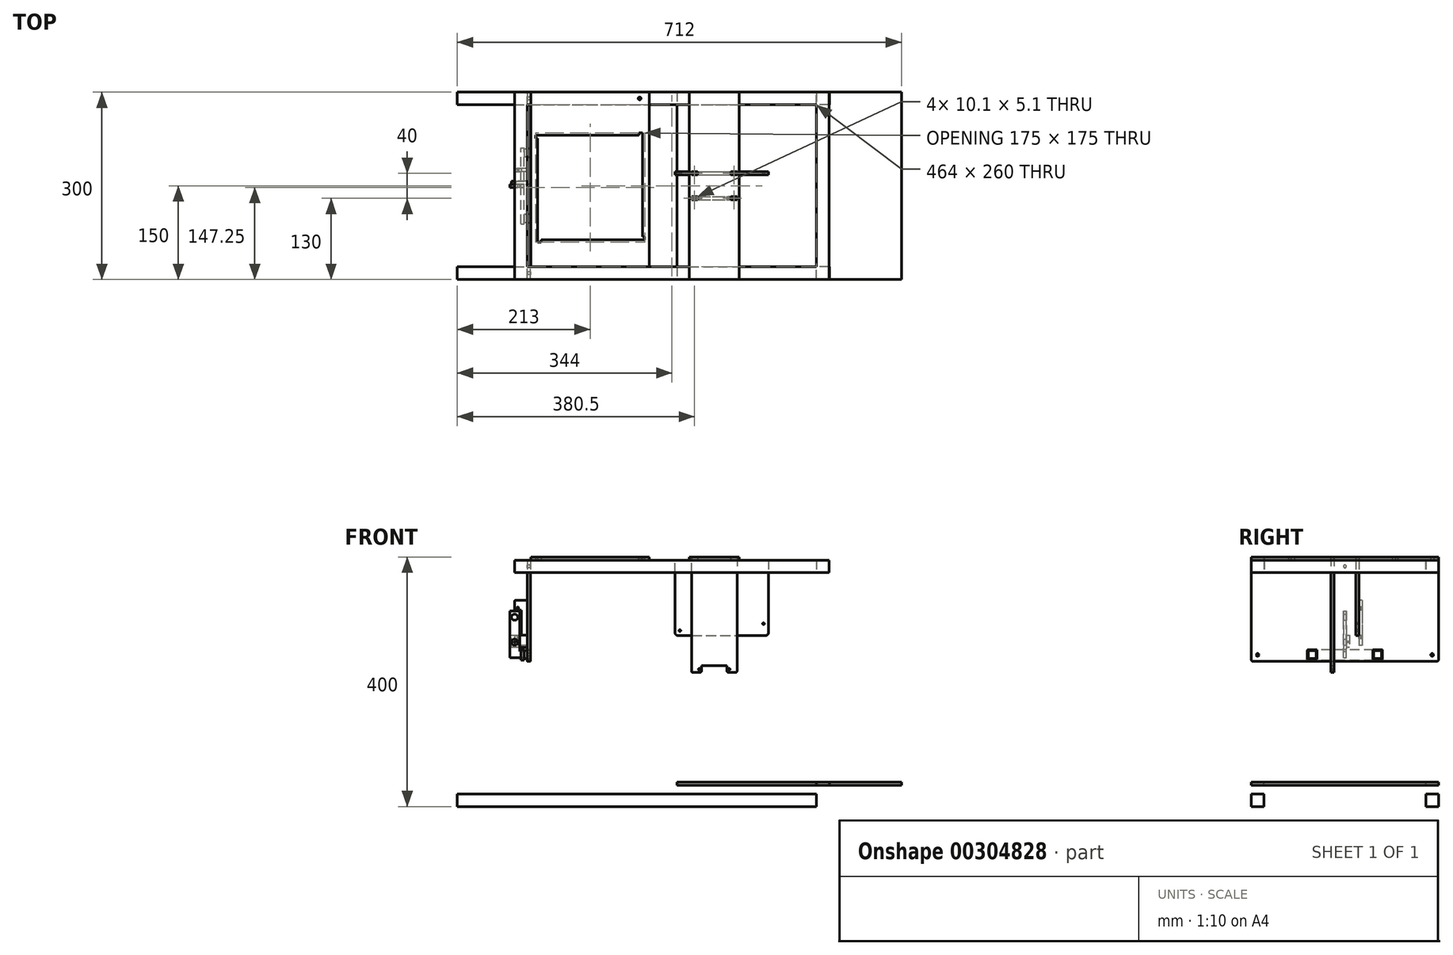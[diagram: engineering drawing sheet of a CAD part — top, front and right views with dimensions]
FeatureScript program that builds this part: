
annotation { "Feature Type Name" : "Feature", "Feature Type Description" : "" }
export const myFeature = defineFeature(function(context is Context, id is Id, definition is map)
    precondition{}
    {
        {
            var Q0;
            Q0=qCreatedBy(makeId("Front.planeOp"),FACE);
            var sketch = newSketch(context, id + "F0", { "sketchPlane" : qUnion([Q0])});
            skLineSegment(sketch, "E0", {"start": v(-53, 64) * mm, "end": v(-53, 180) * mm});
            skCircle(sketch, "E1", {"center": v(-45, 67) * mm, "radius": 1.4 * mm});
            skCircle(sketch, "E2", {"center": v(89, 78) * mm, "radius": 1.4 * mm});
            skLineSegment(sketch, "E3", {"start": v(97, 180) * mm, "end": v(97, 64) * mm});
            skLineSegment(sketch, "E4", {"start": v(-48, 59) * mm, "end": v(92, 59) * mm});
            skArc(sketch, "E5.filletArc", {"start": v(-53, 64) * mm, "mid": v(-51.54, 60.46) * mm, "end": v(-48, 59) * mm});
            skArc(sketch, "E6.filletArc", {"start": v(92, 59) * mm, "mid": v(95.54, 60.46) * mm, "end": v(97, 64) * mm});
            skPoint(sketch, "E7", {"position": v(0, 0) * mm});
            skLineSegment(sketch, "E8", {"start": v(-26.5, 180) * mm, "end": v(-26.5, 185) * mm});
            skLineSegment(sketch, "E9", {"start": v(-26.5, 185) * mm, "end": v(-16.5, 185) * mm});
            skLineSegment(sketch, "E10", {"start": v(-16.5, 185) * mm, "end": v(-16.5, 180) * mm});
            skLineSegment(sketch, "E11", {"start": v(-16.5, 180) * mm, "end": v(36.5, 180) * mm});
            skLineSegment(sketch, "E12", {"start": v(36.5, 180) * mm, "end": v(36.5, 185) * mm});
            skLineSegment(sketch, "E13", {"start": v(36.5, 185) * mm, "end": v(46.5, 185) * mm});
            skLineSegment(sketch, "E14", {"start": v(46.5, 185) * mm, "end": v(46.5, 180) * mm});
            skLineSegment(sketch, "E15", {"start": v(97, 180) * mm, "end": v(46.5, 180) * mm});
            skLineSegment(sketch, "E16", {"start": v(-26.5, 180) * mm, "end": v(-53, 180) * mm});
            skSolve(sketch);
        }
        {
            var Q0;
            Q0=qCreatedBy(makeId("Front.planeOp"),FACE);
            cPlane(context, id + "F1", {"entities" : qUnion([Q0]), "cplaneType" : CPlaneType.OFFSET, "offset" : (17 + 18) * mm, "width" : 150 * mm, "height" : 150 * mm});
        }
        {
            var Q0;
            Q0=qCreatedBy(id+"F1.planeOp",FACE);
            var sketch = newSketch(context, id + "F2", { "sketchPlane" : qUnion([Q0])});
            skCircle(sketch, "E17", {"center": v(-14, 5) * mm, "radius": 1.4 * mm});
            skCircle(sketch, "E18", {"center": v(34, 5) * mm, "radius": 1.4 * mm});
            skLineSegment(sketch, "E19", {"start": v(-24.5, 0) * mm, "end": v(-12.5, 0) * mm});
            skLineSegment(sketch, "E20.trimOffspring", {"start": v(32.5, 0) * mm, "end": v(44.5, 0) * mm});
            skLineSegment(sketch, "E21.top", {"start": v(-10.5, 11) * mm, "end": v(30.5, 11) * mm});
            skLineSegment(sketch, "E21.left", {"start": v(-10.5, 2) * mm, "end": v(-10.5, 11) * mm});
            skLineSegment(sketch, "E21.right", {"start": v(30.5, 2) * mm, "end": v(30.5, 11) * mm});
            skPoint(sketch, "E21.middle", {"position": v(10, 5.5) * mm});
            skLineSegment(sketch, "E22", {"start": v(-26.5, 2) * mm, "end": v(-26.5, 180) * mm});
            skLineSegment(sketch, "E23", {"start": v(46.5, 100) * mm, "end": v(46.5, 2) * mm});
            skPoint(sketch, "E24.visualSharp", {"position": v(-26.5, 0) * mm});
            skArc(sketch, "E24.filletArc", {"start": v(-26.5, 2) * mm, "mid": v(-25.91, 0.59) * mm, "end": v(-24.5, 0) * mm});
            skPoint(sketch, "E25.visualSharp", {"position": v(-10.5, 0) * mm});
            skArc(sketch, "E25.filletArc", {"start": v(-12.5, 0) * mm, "mid": v(-11.09, 0.59) * mm, "end": v(-10.5, 2) * mm});
            skPoint(sketch, "E26.visualSharp", {"position": v(30.5, 0) * mm});
            skArc(sketch, "E26.filletArc", {"start": v(30.5, 2) * mm, "mid": v(31.09, 0.59) * mm, "end": v(32.5, 0) * mm});
            skPoint(sketch, "E27.visualSharp", {"position": v(46.5, 0) * mm});
            skArc(sketch, "E27.filletArc", {"start": v(44.5, 0) * mm, "mid": v(45.91, 0.59) * mm, "end": v(46.5, 2) * mm});
            skLineSegment(sketch, "E28", {"start": v(-26.5, 180) * mm, "end": v(-26.5, 185) * mm});
            skLineSegment(sketch, "E29", {"start": v(-26.5, 185) * mm, "end": v(-16.5, 185) * mm});
            skLineSegment(sketch, "E30", {"start": v(-16.5, 185) * mm, "end": v(-16.5, 180) * mm});
            skLineSegment(sketch, "E31", {"start": v(-16.5, 180) * mm, "end": v(36.5, 180) * mm});
            skLineSegment(sketch, "E32", {"start": v(36.5, 180) * mm, "end": v(36.5, 185) * mm});
            skLineSegment(sketch, "E33", {"start": v(36.5, 185) * mm, "end": v(46.5, 185) * mm});
            skLineSegment(sketch, "E34", {"start": v(46.5, 185) * mm, "end": v(46.5, 100) * mm});
            skLineSegment(sketch, "E35.bottom", {"start": v(-26.5, 200) * mm, "end": v(46.5, 200) * mm});
            skLineSegment(sketch, "E35.top", {"start": v(-26.5, 500) * mm, "end": v(46.5, 500) * mm});
            skLineSegment(sketch, "E35.left", {"start": v(-26.5, 200) * mm, "end": v(-26.5, 327.4) * mm});
            skLineSegment(sketch, "E35.right", {"start": v(46.5, 200) * mm, "end": v(46.5, 327.4) * mm});
            skPoint(sketch, "E36", {"position": v(-26.5, 350) * mm});
            skPoint(sketch, "E37", {"position": v(46.5, 350) * mm});
            skLineSegment(sketch, "E38.bottom", {"start": v(-26.5, 372.6) * mm, "end": v(-16.4, 372.6) * mm});
            skLineSegment(sketch, "E38.top", {"start": v(-26.5, 367.5) * mm, "end": v(-16.4, 367.5) * mm});
            skLineSegment(sketch, "E38.right", {"start": v(-16.4, 372.6) * mm, "end": v(-16.4, 367.5) * mm});
            skLineSegment(sketch, "E39.bottom", {"start": v(46.5, 367.5) * mm, "end": v(36.4, 367.5) * mm});
            skLineSegment(sketch, "E39.top", {"start": v(46.5, 372.6) * mm, "end": v(36.4, 372.6) * mm});
            skLineSegment(sketch, "E39.right", {"start": v(36.4, 367.5) * mm, "end": v(36.4, 372.6) * mm});
            skLineSegment(sketch, "E40.bottom", {"start": v(46.5, 332.5) * mm, "end": v(36.4, 332.5) * mm});
            skLineSegment(sketch, "E40.top", {"start": v(46.5, 327.4) * mm, "end": v(36.4, 327.4) * mm});
            skLineSegment(sketch, "E40.right", {"start": v(36.4, 332.5) * mm, "end": v(36.4, 327.4) * mm});
            skLineSegment(sketch, "E41.bottom", {"start": v(-26.5, 332.5) * mm, "end": v(-16.4, 332.5) * mm});
            skLineSegment(sketch, "E41.top", {"start": v(-26.5, 327.4) * mm, "end": v(-16.4, 327.4) * mm});
            skLineSegment(sketch, "E41.right", {"start": v(-16.4, 332.5) * mm, "end": v(-16.4, 327.4) * mm});
            skLineSegment(sketch, "E42.trimOffspring", {"start": v(-26.5, 372.6) * mm, "end": v(-26.5, 500) * mm});
            skLineSegment(sketch, "E43.trimOffspring", {"start": v(-26.5, 332.5) * mm, "end": v(-26.5, 367.5) * mm});
            skLineSegment(sketch, "E44.trimOffspring", {"start": v(46.5, 372.6) * mm, "end": v(46.5, 500) * mm});
            skLineSegment(sketch, "E45.trimOffspring", {"start": v(46.5, 332.5) * mm, "end": v(46.5, 367.5) * mm});
            skPoint(sketch, "E46", {"position": v(0, 0) * mm});
            skSolve(sketch);
        }
        {
            var Q0;
            Q0=makeQuery(id+"F2.imprint","IMPRINT",FACE,{"disambiguationData":[TD([[makeQuery(id+"F2.imprint","IMPRINT",EDGE,{"derivedFrom":sQuery(id+"F2.wireOp",EDGE,"E17")}),-1.0]])]});
            extrude(context, id + "F3", {"entities" : qUnion([Q0]), "depth" : 5 * mm});
        }
        {
            var Q0;
            Q0=makeQuery(id+"F0.imprint","IMPRINT",FACE,{"disambiguationData":[TD([[makeQuery(id+"F0.imprint","IMPRINT",EDGE,{"derivedFrom":sQuery(id+"F0.wireOp",EDGE,"E0")}),-1.0]])]});
            extrude(context, id + "F4", {"entities" : qUnion([Q0]), "oppositeDirection" : true, "depth" : 5 * mm});
        }
        {
            var Q0;
            Q0=qCreatedBy(id+"F1.planeOp",FACE);
            var sketch = newSketch(context, id + "F5", { "sketchPlane" : qUnion([Q0])});
            skPoint(sketch, "E47", {"position": v(-12.33, -156.3) * mm});
            skPoint(sketch, "E48", {"position": v(-265.6, 28.34) * mm});
            skPoint(sketch, "E49", {"position": v(185.46, 123.56) * mm});
            skLineSegment(sketch, "E50.bottom", {"start": v(-17.83, -156.3) * mm, "end": v(3.17, -156.3) * mm});
            skLineSegment(sketch, "E50.top", {"start": v(-17.83, -151.3) * mm, "end": v(3.17, -151.3) * mm});
            skLineSegment(sketch, "E50.left", {"start": v(-17.83, -156.3) * mm, "end": v(-17.83, -151.3) * mm});
            skLineSegment(sketch, "E50.right", {"start": v(3.17, -156.3) * mm, "end": v(3.17, -151.3) * mm});
            skCircle(sketch, "E51", {"center": v(185.46, 123.56) * mm, "radius": 6 * mm});
            skPoint(sketch, "E52", {"position": v(132.1, 171.6) * mm});
            skCircle(sketch, "E53", {"center": v(132.1, 171.6) * mm, "radius": 6 * mm});
            skSolve(sketch);
        }
        {
            var Q0;
            Q0=qCreatedBy(makeId("Top.planeOp"),FACE);
            cPlane(context, id + "F6", {"entities" : qUnion([Q0]), "cplaneType" : CPlaneType.OFFSET, "offset" : 176 * mm, "oppositeDirection" : true, "width" : 150 * mm, "height" : 150 * mm});
        }
        {
            var Q0;
            Q0=qCreatedBy(id+"F6.planeOp",FACE);
            var sketch = newSketch(context, id + "F7", { "sketchPlane" : qUnion([Q0])});
            skPoint(sketch, "E54", {"position": v(310, -10) * mm});
            skLineSegment(sketch, "E55.top", {"start": v(173.5, 132.5) * mm, "end": v(-50, 132.5) * mm});
            skLineSegment(sketch, "E56.top", {"start": v(173.5, -167.5) * mm, "end": v(-50, -167.5) * mm});
            skLineSegment(sketch, "E57", {"start": v(-50, 132.5) * mm, "end": v(-50, -167.5) * mm});
            skLineSegment(sketch, "E58", {"start": v(310, 132.5) * mm, "end": v(310, -167.5) * mm});
            skPoint(sketch, "E59", {"position": v(310, -17.5) * mm});
            skLineSegment(sketch, "E60.top", {"start": v(194.5, 112.5) * mm, "end": v(173.5, 112.5) * mm});
            skLineSegment(sketch, "E60.right", {"start": v(173.5, 132.5) * mm, "end": v(173.5, 112.5) * mm});
            skPoint(sketch, "E60.left.start.orphan", {"position": v(310, 132.5) * mm});
            skLineSegment(sketch, "E61.top", {"start": v(194.5, -147.5) * mm, "end": v(173.5, -147.5) * mm});
            skLineSegment(sketch, "E61.right", {"start": v(173.5, -167.5) * mm, "end": v(173.5, -147.5) * mm});
            skPoint(sketch, "E61.left.start.orphan", {"position": v(310, -167.5) * mm});
            skPoint(sketch, "E62", {"position": v(-50, -17.5) * mm});
            skLineSegment(sketch, "E63", {"start": v(194.5, 112.5) * mm, "end": v(194.5, 132.5) * mm});
            skLineSegment(sketch, "E64", {"start": v(194.5, 132.5) * mm, "end": v(310, 132.5) * mm});
            skLineSegment(sketch, "E65", {"start": v(194.5, -147.5) * mm, "end": v(194.5, -167.5) * mm});
            skLineSegment(sketch, "E66", {"start": v(194.5, -167.5) * mm, "end": v(310, -167.5) * mm});
            skSolve(sketch);
        }
        {
            var Q0;
            Q0=qCreatedBy(makeId("Top.planeOp"),FACE);
            cPlane(context, id + "F8", {"entities" : qUnion([Q0]), "cplaneType" : CPlaneType.OFFSET, "offset" : 160 * mm, "width" : 150 * mm, "height" : 150 * mm});
        }
        {
            var Q0;
            Q0=qCreatedBy(id+"F8.planeOp",FACE);
            var sketch = newSketch(context, id + "F9", { "sketchPlane" : qUnion([Q0])});
            skLineSegment(sketch, "E67.bottom", {"start": v(-290, 112.5) * mm, "end": v(174, 112.5) * mm});
            skLineSegment(sketch, "E67.top", {"start": v(-290, -147.5) * mm, "end": v(174, -147.5) * mm});
            skLineSegment(sketch, "E67.left", {"start": v(-290, 112.5) * mm, "end": v(-290, -147.5) * mm});
            skLineSegment(sketch, "E67.right", {"start": v(174, 112.5) * mm, "end": v(174, -147.5) * mm});
            skLineSegment(sketch, "E68.bottom", {"start": v(-310, 132.5) * mm, "end": v(194, 132.5) * mm});
            skLineSegment(sketch, "E68.top", {"start": v(-310, -167.5) * mm, "end": v(194, -167.5) * mm});
            skLineSegment(sketch, "E68.left", {"start": v(-310, 132.5) * mm, "end": v(-310, -167.5) * mm});
            skLineSegment(sketch, "E68.right", {"start": v(194, 132.5) * mm, "end": v(194, -167.5) * mm});
            skLineSegment(sketch, "E69.bottom", {"start": v(-290, 112.5) * mm, "end": v(-310, 112.5) * mm});
            skLineSegment(sketch, "E69.top", {"start": v(-290, 132.5) * mm, "end": v(-310, 132.5) * mm});
            skLineSegment(sketch, "E69.left", {"start": v(-290, 112.5) * mm, "end": v(-290, 132.5) * mm});
            skLineSegment(sketch, "E69.right", {"start": v(-310, 112.5) * mm, "end": v(-310, 132.5) * mm});
            skLineSegment(sketch, "E70.bottom", {"start": v(-290, -147.5) * mm, "end": v(-310, -147.5) * mm});
            skLineSegment(sketch, "E70.top", {"start": v(-290, -167.5) * mm, "end": v(-310, -167.5) * mm});
            skLineSegment(sketch, "E70.left", {"start": v(-290, -147.5) * mm, "end": v(-290, -167.5) * mm});
            skLineSegment(sketch, "E70.right", {"start": v(-310, -147.5) * mm, "end": v(-310, -167.5) * mm});
            skLineSegment(sketch, "E71.bottom", {"start": v(194, -167.5) * mm, "end": v(174, -167.5) * mm});
            skLineSegment(sketch, "E71.top", {"start": v(194, -147.5) * mm, "end": v(174, -147.5) * mm});
            skLineSegment(sketch, "E71.left", {"start": v(194, -167.5) * mm, "end": v(194, -147.5) * mm});
            skLineSegment(sketch, "E71.right", {"start": v(174, -167.5) * mm, "end": v(174, -147.5) * mm});
            skLineSegment(sketch, "E72.bottom", {"start": v(194, 132.5) * mm, "end": v(174, 132.5) * mm});
            skLineSegment(sketch, "E72.top", {"start": v(194, 112.5) * mm, "end": v(174, 112.5) * mm});
            skLineSegment(sketch, "E72.left", {"start": v(194, 132.5) * mm, "end": v(194, 112.5) * mm});
            skLineSegment(sketch, "E72.right", {"start": v(174, 132.5) * mm, "end": v(174, 112.5) * mm});
            skPoint(sketch, "E73", {"position": v(-285, -35) * mm});
            skPoint(sketch, "E74", {"position": v(-290, -35) * mm});
            skLineSegment(sketch, "E75", {"start": v(0, 0) * mm, "end": v(0, -35) * mm});
            skPoint(sketch, "E76", {"position": v(0, -17.5) * mm});
            skSolve(sketch);
        }
        {
            var Q0;
            Q0=qSketchRegion(id+"F9",true);
            var Q1;
            {var subQ0=sQuery(id+"F9.wireOp",EDGE,"2Zz8rPLi-nCmv-pbZF-Ckmh-jJj1cyJJyCpR");Q1=makeQuery(id+"F9.imprint","IMPRINT",FACE,{"disambiguationData":[TD([[makeQuery(id+"F9.imprint","IMPRINT",EDGE,{"derivedFrom":subQ0}),-1.0]])]});}
            extrude(context, id + "F10", {"entities" : qUnion([Q0, Q1]), "operationType" : NewBodyOperationType.ADD, "depth" : 20 * mm});
        }
        {
            var Q0;
            Q0=qSketchRegion(id+"F7",true);
            extrude(context, id + "F11", {"entities" : qUnion([Q0]), "operationType" : NewBodyOperationType.ADD, "oppositeDirection" : true, "depth" : 5 * mm});
        }
        {
            var Q0;
            Q0=sQuery(id+"F9.wireOp",EDGE,"E70.bottom");
            var Q1;
            Q1=sQuery(id+"F9.wireOp",EDGE,"E70.left");
            var Q2;
            Q2=sQuery(id+"F9.wireOp",EDGE,"E70.top");
            var Q3;
            Q3=sQuery(id+"F9.wireOp",EDGE,"E70.right");
            var Q4;
            Q4=sQuery(id+"F9.wireOp",EDGE,"E71.top");
            var Q5;
            Q5=sQuery(id+"F9.wireOp",EDGE,"E71.left");
            var Q6;
            Q6=sQuery(id+"F9.wireOp",EDGE,"E71.bottom");
            var Q7;
            Q7=sQuery(id+"F9.wireOp",EDGE,"E71.right");
            var Q8;
            Q8=sQuery(id+"F9.wireOp",EDGE,"E72.right");
            var Q9;
            Q9=sQuery(id+"F9.wireOp",EDGE,"E72.left");
            var Q10;
            Q10=sQuery(id+"F9.wireOp",EDGE,"E72.bottom");
            var Q11;
            Q11=sQuery(id+"F9.wireOp",EDGE,"E72.top");
            var Q12;
            Q12=sQuery(id+"F9.wireOp",EDGE,"E69.bottom");
            var Q13;
            Q13=sQuery(id+"F9.wireOp",EDGE,"E69.top");
            var Q14;
            Q14=sQuery(id+"F9.wireOp",EDGE,"E69.right");
            var Q15;
            Q15=sQuery(id+"F9.wireOp",EDGE,"E69.left");
            extrude(context, id + "F12", {"bodyType" : ToolBodyType.SURFACE, "surfaceEntities" : qUnion([Q0, Q1, Q2, Q3, Q4, Q5, Q6, Q7, Q8, Q9, Q10, Q11, Q12, Q13, Q14, Q15]), "oppositeDirection" : true, "depth" : 500 * mm});
        }
        {
            var Q0;
            Q0=makeQuery(id+"F12.opExtrude","SWEPT_FACE",FACE,{"disambiguationData":[OSD([sQuery(id+"F9.wireOp",EDGE,"E71.right")])]});
            var sketch = newSketch(context, id + "F13", { "sketchPlane" : qUnion([Q0])});
            skLineSegment(sketch, "E77.bottom", {"start": v(-167.5, -195) * mm, "end": v(-147.5, -195) * mm});
            skLineSegment(sketch, "E77.top", {"start": v(-167.5, -215) * mm, "end": v(-147.5, -215) * mm});
            skLineSegment(sketch, "E77.left", {"start": v(-167.5, -195) * mm, "end": v(-167.5, -215) * mm});
            skLineSegment(sketch, "E77.right", {"start": v(-147.5, -195) * mm, "end": v(-147.5, -215) * mm});
            skLineSegment(sketch, "E78.bottom", {"start": v(112.5, -195) * mm, "end": v(132.5, -195) * mm});
            skLineSegment(sketch, "E78.top", {"start": v(112.5, -215) * mm, "end": v(132.5, -215) * mm});
            skLineSegment(sketch, "E78.left", {"start": v(112.5, -195) * mm, "end": v(112.5, -215) * mm});
            skLineSegment(sketch, "E78.right", {"start": v(132.5, -195) * mm, "end": v(132.5, -215) * mm});
            skSolve(sketch);
        }
        {
            var Q0;
            Q0=qSketchRegion(id+"F13",true);
            extrude(context, id + "F14", {"entities" : qUnion([Q0]), "operationType" : NewBodyOperationType.ADD, "oppositeDirection" : true, "depth" : 576 * mm});
        }
        {
            var Q0;
            {var subQ0=sQuery(id+"F9.wireOp",EDGE,"E67.left");Q0=makeQuery(id+"F10.opExtrude","SWEPT_FACE",FACE,{"disambiguationData":[OSD([subQ0]),TDD([makeQuery(id+"F9.imprint","IMPRINT",EDGE,{"disambiguationData":[TD([[makeQuery(id+"F9.imprint","INTERSECT",VERTEX,{"derivedFrom":[subQ0,sQuery(id+"F9.wireOp",EDGE,"KOu01N03-8pH1-00IH-skWm-jKx7iMjYsmLb")]}),-1.0]])],"derivedFrom":subQ0})])]});}
            var sketch = newSketch(context, id + "F15", { "sketchPlane" : qUnion([Q0])});
            skPoint(sketch, "E79", {"position": v(-80, 28) * mm});
            skPoint(sketch, "E80", {"position": v(59, 28) * mm});
            skLineSegment(sketch, "E81.bottom", {"start": v(-165.5, 18) * mm, "end": v(130.5, 18) * mm});
            skLineSegment(sketch, "E81.left", {"start": v(-167.5, 20) * mm, "end": v(-167.5, 160) * mm});
            skLineSegment(sketch, "E81.right", {"start": v(132.5, 20) * mm, "end": v(132.5, 160) * mm});
            skPoint(sketch, "E82.visualSharp", {"position": v(-167.5, 18) * mm});
            skArc(sketch, "E82.filletArc", {"start": v(-167.5, 20) * mm, "mid": v(-166.91, 18.59) * mm, "end": v(-165.5, 18) * mm});
            skPoint(sketch, "E83.visualSharp", {"position": v(132.5, 18) * mm});
            skArc(sketch, "E83.filletArc", {"start": v(130.5, 18) * mm, "mid": v(131.91, 18.59) * mm, "end": v(132.5, 20) * mm});
            skLineSegment(sketch, "E84.top", {"start": v(-167.5, 160) * mm, "end": v(-147, 160) * mm});
            skLineSegment(sketch, "E84.right", {"start": v(-147, 180) * mm, "end": v(-147, 160) * mm});
            skLineSegment(sketch, "E85.top", {"start": v(132.5, 160) * mm, "end": v(112, 160) * mm});
            skLineSegment(sketch, "E85.right", {"start": v(112, 180) * mm, "end": v(112, 160) * mm});
            skPoint(sketch, "E86.middle", {"position": v(-17.5, 170) * mm});
            skPoint(sketch, "E86.middle.positionSnap0", {"position": v(-17.5, 180) * mm});
            skPoint(sketch, "E86.centerSnap0", {"position": v(-17.5, 180) * mm});
            skPoint(sketch, "E87.orphan", {"position": v(-167.5, 180) * mm});
            skLineSegment(sketch, "E88.trimOffspring", {"start": v(-147, 180) * mm, "end": v(112, 180) * mm});
            skPoint(sketch, "E89.orphan", {"position": v(132.5, 180) * mm});
            skCircle(sketch, "E90", {"center": v(-157.5, 28) * mm, "radius": 2.25 * mm});
            skCircle(sketch, "E91", {"center": v(122.5, 28) * mm, "radius": 2.25 * mm});
            skCircle(sketch, "E92", {"center": v(-17.5, 170) * mm, "radius": 2.25 * mm});
            skLineSegment(sketch, "E93.bottom", {"start": v(42.5, 36) * mm, "end": v(27.5, 36) * mm});
            skLineSegment(sketch, "E93.top", {"start": v(42.5, 21) * mm, "end": v(27.5, 21) * mm});
            skLineSegment(sketch, "E93.left", {"start": v(42.5, 36) * mm, "end": v(42.5, 21) * mm});
            skLineSegment(sketch, "E93.right", {"start": v(27.5, 36) * mm, "end": v(27.5, 21) * mm});
            skLineSegment(sketch, "E94.bottom", {"start": v(-62.5, 21) * mm, "end": v(-77.5, 21) * mm});
            skLineSegment(sketch, "E94.top", {"start": v(-62.5, 36) * mm, "end": v(-77.5, 36) * mm});
            skLineSegment(sketch, "E94.left", {"start": v(-62.5, 21) * mm, "end": v(-62.5, 36) * mm});
            skLineSegment(sketch, "E94.right", {"start": v(-77.5, 21) * mm, "end": v(-77.5, 36) * mm});
            skSolve(sketch);
        }
        {
            var Q0;
            Q0=makeQuery(id+"F10.opExtrude","CAP_FACE",FACE,{"disambiguationData":[OSD([sQuery(id+"F9.wireOp",EDGE,"E67.bottom"),sQuery(id+"F9.wireOp",EDGE,"E67.top"),sQuery(id+"F9.wireOp",EDGE,"E67.left"),sQuery(id+"F9.wireOp",EDGE,"E67.right"),sQuery(id+"F9.wireOp",EDGE,"E68.bottom"),sQuery(id+"F9.wireOp",EDGE,"E68.top"),sQuery(id+"F9.wireOp",EDGE,"E68.left"),sQuery(id+"F9.wireOp",EDGE,"E68.right"),sQuery(id+"F9.wireOp",EDGE,"2Zz8rPLi-nCmv-pbZF-Ckmh-jJj1cyJJyCpR"),sQuery(id+"F9.wireOp",EDGE,"KOu01N03-8pH1-00IH-skWm-jKx7iMjYsmLb"),sQuery(id+"F9.wireOp",EDGE,"E69.top"),sQuery(id+"F9.wireOp",EDGE,"E69.right"),sQuery(id+"F9.wireOp",EDGE,"E70.top"),sQuery(id+"F9.wireOp",EDGE,"E70.right"),sQuery(id+"F9.wireOp",EDGE,"E71.bottom"),sQuery(id+"F9.wireOp",EDGE,"E71.left"),sQuery(id+"F9.wireOp",EDGE,"E72.bottom"),sQuery(id+"F9.wireOp",EDGE,"E72.left")])],"isStart":false});
            var sketch = newSketch(context, id + "F16", { "sketchPlane" : qUnion([Q0])});
            skLineSegment(sketch, "E95.bottom", {"start": v(-273, -104.25) * mm, "end": v(-273, 58.25) * mm});
            skLineSegment(sketch, "E95.top", {"start": v(-105, -98.75) * mm, "end": v(-105, 63.75) * mm});
            skLineSegment(sketch, "E95.left", {"start": v(-267.5, -104.25) * mm, "end": v(-105, -104.25) * mm});
            skLineSegment(sketch, "E95.right", {"start": v(-273, 63.75) * mm, "end": v(-110.5, 63.75) * mm});
            skLineSegment(sketch, "E96", {"start": v(-273, -104.25) * mm, "end": v(-273, -107.75) * mm});
            skLineSegment(sketch, "E97", {"start": v(-273, -107.75) * mm, "end": v(-267.5, -107.75) * mm});
            skLineSegment(sketch, "E98", {"start": v(-267.5, -107.75) * mm, "end": v(-267.5, -104.25) * mm});
            skLineSegment(sketch, "E99", {"start": v(-105, -104.25) * mm, "end": v(-101.5, -104.25) * mm});
            skLineSegment(sketch, "E100", {"start": v(-101.5, -104.25) * mm, "end": v(-101.5, -98.75) * mm});
            skLineSegment(sketch, "E101", {"start": v(-101.5, -98.75) * mm, "end": v(-105, -98.75) * mm});
            skLineSegment(sketch, "E102", {"start": v(-105, 63.75) * mm, "end": v(-105, 67.25) * mm});
            skLineSegment(sketch, "E103", {"start": v(-105, 67.25) * mm, "end": v(-110.5, 67.25) * mm});
            skLineSegment(sketch, "E104", {"start": v(-110.5, 67.25) * mm, "end": v(-110.5, 63.75) * mm});
            skLineSegment(sketch, "E105", {"start": v(-273, 63.75) * mm, "end": v(-276.5, 63.75) * mm});
            skLineSegment(sketch, "E106", {"start": v(-276.5, 63.75) * mm, "end": v(-276.5, 58.25) * mm});
            skLineSegment(sketch, "E107", {"start": v(-276.5, 58.25) * mm, "end": v(-273, 58.25) * mm});
            skLineSegment(sketch, "E108.right", {"start": v(-284, 132.5) * mm, "end": v(-94, 132.5) * mm});
            skCircle(sketch, "E109", {"center": v(-109.6, 122.5) * mm, "radius": 2.25 * mm});
            skLineSegment(sketch, "E110", {"start": v(-94, 132.5) * mm, "end": v(-94, -167.5) * mm});
            skLineSegment(sketch, "E111", {"start": v(-284, -167.5) * mm, "end": v(-94, -167.5) * mm});
            skLineSegment(sketch, "E112", {"start": v(-284, 132.5) * mm, "end": v(-284, -167.5) * mm});
            skPoint(sketch, "E113", {"position": v(-273, -23) * mm});
            skPoint(sketch, "E114", {"position": v(-105, -17.5) * mm});
            skSolve(sketch);
        }
        {
            var Q0;
            Q0=makeQuery(id+"F16.imprint","IMPRINT",FACE,{"disambiguationData":[TD([[makeQuery(id+"F16.imprint","IMPRINT",EDGE,{"derivedFrom":sQuery(id+"F16.wireOp",EDGE,"E95.bottom")}),1.0]])]});
            var Q1;
            {var subQ0=sQuery(id+"F16.wireOp",EDGE,"E111");Q1=makeQuery(id+"F16.imprint","IMPRINT",FACE,{"disambiguationData":[TD([[makeQuery(id+"F16.imprint","IMPRINT",EDGE,{"derivedFrom":subQ0}),-1.0]])]});}
            var Q2;
            {var subQ1=sQuery(id+"F16.wireOp",EDGE,"E108.right");Q2=makeQuery(id+"F16.imprint","IMPRINT",FACE,{"disambiguationData":[TD([[makeQuery(id+"F16.imprint","IMPRINT",EDGE,{"derivedFrom":subQ1}),1.0]])]});}
            var Q3;
            Q3=makeQuery(id+"F16.imprint","IMPRINT",FACE,{"disambiguationData":[TD([[makeQuery(id+"F16.imprint","IMPRINT",EDGE,{"derivedFrom":sQuery(id+"F16.wireOp",EDGE,"E109")}),-1.0]])]});
            var Q4;
            {var subQ0=sQuery(id+"F16.wireOp",EDGE,"E108.right");Q4=makeQuery(id+"F16.imprint","IMPRINT",FACE,{"disambiguationData":[TD([[makeQuery(id+"F16.imprint","IMPRINT",EDGE,{"derivedFrom":subQ0}),-1.0]])]});}
            extrude(context, id + "F17", {"entities" : qUnion([Q0, Q1, Q2, Q3, Q4]), "depth" : 5 * mm});
        }
        {
            var Q0;
            Q0=makeQuery(id+"F10.opExtrude","CAP_FACE",FACE,{"disambiguationData":[OSD([sQuery(id+"F9.wireOp",EDGE,"E67.bottom"),sQuery(id+"F9.wireOp",EDGE,"E67.top"),sQuery(id+"F9.wireOp",EDGE,"E67.left"),sQuery(id+"F9.wireOp",EDGE,"E67.right"),sQuery(id+"F9.wireOp",EDGE,"E68.bottom"),sQuery(id+"F9.wireOp",EDGE,"E68.top"),sQuery(id+"F9.wireOp",EDGE,"E68.left"),sQuery(id+"F9.wireOp",EDGE,"E68.right"),sQuery(id+"F9.wireOp",EDGE,"E69.top"),sQuery(id+"F9.wireOp",EDGE,"E69.right"),sQuery(id+"F9.wireOp",EDGE,"E70.top"),sQuery(id+"F9.wireOp",EDGE,"E70.right"),sQuery(id+"F9.wireOp",EDGE,"E71.bottom"),sQuery(id+"F9.wireOp",EDGE,"E71.left"),sQuery(id+"F9.wireOp",EDGE,"E72.bottom"),sQuery(id+"F9.wireOp",EDGE,"E72.left")])],"isStart":false});
            var sketch = newSketch(context, id + "F18", { "sketchPlane" : qUnion([Q0])});
            skPoint(sketch, "E115", {"position": v(-36, -17.5) * mm});
            skPoint(sketch, "E116", {"position": v(36, -17.5) * mm});
            skLineSegment(sketch, "E117.bottom", {"start": v(-26.55, 5.05) * mm, "end": v(-16.45, 5.05) * mm});
            skLineSegment(sketch, "E117.top", {"start": v(-26.55, -0.05) * mm, "end": v(-16.45, -0.05) * mm});
            skLineSegment(sketch, "E117.right", {"start": v(-16.45, 5.05) * mm, "end": v(-16.45, -0.05) * mm});
            skLineSegment(sketch, "E118.bottom", {"start": v(46.55, -0.05) * mm, "end": v(36.45, -0.05) * mm});
            skLineSegment(sketch, "E118.top", {"start": v(46.55, 5.05) * mm, "end": v(36.45, 5.05) * mm});
            skLineSegment(sketch, "E118.right", {"start": v(36.45, -0.05) * mm, "end": v(36.45, 5.05) * mm});
            skLineSegment(sketch, "E119.bottom", {"start": v(46.55, -34.95) * mm, "end": v(36.45, -34.95) * mm});
            skLineSegment(sketch, "E119.top", {"start": v(46.55, -40.05) * mm, "end": v(36.45, -40.05) * mm});
            skLineSegment(sketch, "E119.right", {"start": v(36.45, -34.95) * mm, "end": v(36.45, -40.05) * mm});
            skLineSegment(sketch, "E120.bottom", {"start": v(-26.55, -34.95) * mm, "end": v(-16.45, -34.95) * mm});
            skLineSegment(sketch, "E120.top", {"start": v(-26.55, -40.05) * mm, "end": v(-16.45, -40.05) * mm});
            skLineSegment(sketch, "E120.right", {"start": v(-16.45, -34.95) * mm, "end": v(-16.45, -40.05) * mm});
            skLineSegment(sketch, "E121", {"start": v(46.55, -40.05) * mm, "end": v(46.55, -34.95) * mm});
            skLineSegment(sketch, "E122", {"start": v(46.55, 5.05) * mm, "end": v(46.55, -0.05) * mm});
            skLineSegment(sketch, "E123", {"start": v(-26.55, 5.05) * mm, "end": v(-26.55, -0.05) * mm});
            skLineSegment(sketch, "E124", {"start": v(-26.55, -34.95) * mm, "end": v(-26.55, -40.05) * mm});
            skLineSegment(sketch, "E125.bottom", {"start": v(50, -167.5) * mm, "end": v(-30, -167.5) * mm});
            skLineSegment(sketch, "E125.top", {"start": v(50, 132.5) * mm, "end": v(-30, 132.5) * mm});
            skLineSegment(sketch, "E125.left", {"start": v(50, -167.5) * mm, "end": v(50, 132.5) * mm});
            skLineSegment(sketch, "E125.right", {"start": v(-30, -167.5) * mm, "end": v(-30, 132.5) * mm});
            skPoint(sketch, "E126", {"position": v(0, 0) * mm});
            skSolve(sketch);
        }
        {
            var Q0;
            Q0 = qSketchRegion(id + "F18", true);
            extrude(context, id + "F19", {"entities" : qUnion([Q0]), "depth" : 5 * mm});
        }
        {
            var Q0;
            Q0=qCreatedBy(makeId("Right.planeOp"),FACE);
            cPlane(context, id + "F20", {"entities" : qUnion([Q0]), "cplaneType" : CPlaneType.OFFSET, "offset" : 295 * mm, "oppositeDirection" : true, "width" : 150 * mm, "height" : 150 * mm});
        }
        {
            var Q0;
            Q0=qCreatedBy(id+"F20.planeOp",FACE);
            var sketch = newSketch(context, id + "F21", { "sketchPlane" : qUnion([Q0])});
            skLineSegment(sketch, "E127.bottom", {"start": v(41.5, 35) * mm, "end": v(28.5, 35) * mm});
            skLineSegment(sketch, "E127.top", {"start": v(41.5, 22) * mm, "end": v(28.5, 22) * mm});
            skLineSegment(sketch, "E127.left", {"start": v(41.5, 35) * mm, "end": v(41.5, 22) * mm});
            skLineSegment(sketch, "E127.right", {"start": v(28.5, 35) * mm, "end": v(28.5, 22) * mm});
            skLineSegment(sketch, "E128.bottom", {"start": v(-63.5, 22) * mm, "end": v(-76.5, 22) * mm});
            skLineSegment(sketch, "E128.top", {"start": v(-63.5, 35) * mm, "end": v(-76.5, 35) * mm});
            skLineSegment(sketch, "E128.left", {"start": v(-63.5, 22) * mm, "end": v(-63.5, 35) * mm});
            skLineSegment(sketch, "E128.right", {"start": v(-76.5, 22) * mm, "end": v(-76.5, 35) * mm});
            skSolve(sketch);
        }
        {
            var Q0;
            Q0 = qSketchRegion(id + "F15", true);
            extrude(context, id + "F22", {"entities" : qUnion([Q0]), "depth" : 5 * mm});
        }
        {
            var Q0;
            Q0 = qSketchRegion(id + "F21", true);
            extrude(context, id + "F23", {"entities" : qUnion([Q0]), "depth" : 10 * mm});
        }
        {
            var Q0;
            Q0=qCreatedBy(id+"F20.planeOp",FACE);
            var sketch = newSketch(context, id + "F24", { "sketchPlane" : qUnion([Q0])});
            skLineSegment(sketch, "E129.bottom", {"start": v(-78.5, 20) * mm, "end": v(43.5, 20) * mm});
            skLineSegment(sketch, "E129.top", {"start": v(-78.5, 37) * mm, "end": v(43.5, 37) * mm});
            skLineSegment(sketch, "E129.left", {"start": v(-78.5, 20) * mm, "end": v(-78.5, 37) * mm});
            skLineSegment(sketch, "E129.right", {"start": v(43.5, 20) * mm, "end": v(43.5, 37) * mm});
            skPoint(sketch, "E129.middle", {"position": v(-17.5, 28.5) * mm});
            skLineSegment(sketch, "E130.bottom", {"start": v(-20, 23.5) * mm, "end": v(-15, 23.5) * mm});
            skLineSegment(sketch, "E130.top", {"start": v(-20, 33.5) * mm, "end": v(-15, 33.5) * mm});
            skLineSegment(sketch, "E130.left", {"start": v(-20, 23.5) * mm, "end": v(-20, 33.5) * mm});
            skLineSegment(sketch, "E130.right", {"start": v(-15, 23.5) * mm, "end": v(-15, 33.5) * mm});
            skSolve(sketch);
        }
        {
            var Q0;
            Q0=makeQuery(id+"F24.imprint","IMPRINT",FACE,{"disambiguationData":[TD([[makeQuery(id+"F24.imprint","IMPRINT",EDGE,{"derivedFrom":sQuery(id+"F24.wireOp",EDGE,"E129.bottom")}),1.0]])]});
            extrude(context, id + "F25", {"entities" : qUnion([Q0]), "oppositeDirection" : true, "depth" : 5 * mm});
        }
        {
            var Q0;
            Q0=qCreatedBy(makeId("Front.planeOp"),FACE);
            cPlane(context, id + "F26", {"entities" : qUnion([Q0]), "cplaneType" : CPlaneType.OFFSET, "offset" : 15 * mm, "width" : 150 * mm, "height" : 150 * mm});
        }
        {
            var Q0;
            Q0=qCreatedBy(id+"F26.planeOp",FACE);
            var sketch = newSketch(context, id + "F27", { "sketchPlane" : qUnion([Q0])});
            skLineSegment(sketch, "E131.bottom", {"start": v(-290, 40) * mm, "end": v(-315, 40) * mm});
            skLineSegment(sketch, "E131.top", {"start": v(-290, 60) * mm, "end": v(-315, 60) * mm});
            skLineSegment(sketch, "E131.left", {"start": v(-290, 45) * mm, "end": v(-290, 55) * mm});
            skLineSegment(sketch, "E131.right", {"start": v(-315, 40) * mm, "end": v(-315, 60) * mm});
            skCircle(sketch, "E132", {"center": v(-310, 48.5) * mm, "radius": 0.9 * mm});
            skLineSegment(sketch, "E133.bottom", {"start": v(-290, 60) * mm, "end": v(-285, 60) * mm});
            skLineSegment(sketch, "E133.top", {"start": v(-290, 55) * mm, "end": v(-285, 55) * mm});
            skLineSegment(sketch, "E133.right", {"start": v(-285, 60) * mm, "end": v(-285, 55) * mm});
            skLineSegment(sketch, "E134.bottom", {"start": v(-290, 40) * mm, "end": v(-285, 40) * mm});
            skLineSegment(sketch, "E134.top", {"start": v(-290, 45) * mm, "end": v(-285, 45) * mm});
            skLineSegment(sketch, "E134.right", {"start": v(-285, 40) * mm, "end": v(-285, 45) * mm});
            skSolve(sketch);
        }
        {
            var Q0;
            Q0=makeQuery(id+"F27.imprint","IMPRINT",FACE,{"disambiguationData":[TD([[makeQuery(id+"F27.imprint","IMPRINT",EDGE,{"derivedFrom":sQuery(id+"F27.wireOp",EDGE,"E131.bottom")}),-1.0]])]});
            extrude(context, id + "F28", {"entities" : qUnion([Q0]), "operationType" : NewBodyOperationType.ADD, "oppositeDirection" : true, "depth" : 5 * mm});
        }
        {
            var Q0;
            Q0=qCreatedBy(id+"F26.planeOp",FACE);
            cPlane(context, id + "F29", {"entities" : qUnion([Q0]), "cplaneType" : CPlaneType.OFFSET, "offset" : 20 * mm, "oppositeDirection" : true, "width" : 150 * mm, "height" : 150 * mm});
        }
        {
            var Q0;
            Q0=qCreatedBy(id+"F29.planeOp",FACE);
            var sketch = newSketch(context, id + "F30", { "sketchPlane" : qUnion([Q0])});
            skCircle(sketch, "E135", {"center": v(-305, 103.4) * mm, "radius": 1.4 * mm});
            skCircle(sketch, "E136", {"center": v(-305, 55.4) * mm, "radius": 1.4 * mm});
            skLineSegment(sketch, "E137", {"start": v(-310, 113.9) * mm, "end": v(-310, 101.9) * mm});
            skLineSegment(sketch, "E138.trimOffspring", {"start": v(-310, 56.9) * mm, "end": v(-310, 44.9) * mm});
            skLineSegment(sketch, "E139.top", {"start": v(-299, 99.9) * mm, "end": v(-299, 58.9) * mm});
            skLineSegment(sketch, "E139.left", {"start": v(-308, 99.9) * mm, "end": v(-299, 99.9) * mm});
            skLineSegment(sketch, "E139.right", {"start": v(-308, 58.9) * mm, "end": v(-299, 58.9) * mm});
            skPoint(sketch, "E139.middle", {"position": v(-304.5, 79.4) * mm});
            skLineSegment(sketch, "E140", {"start": v(-308, 115.9) * mm, "end": v(-290, 115.9) * mm});
            skLineSegment(sketch, "E141", {"start": v(-290, 42.9) * mm, "end": v(-308, 42.9) * mm});
            skPoint(sketch, "E142.visualSharp", {"position": v(-310, 115.9) * mm});
            skArc(sketch, "E142.filletArc", {"start": v(-308, 115.9) * mm, "mid": v(-309.41, 115.31) * mm, "end": v(-310, 113.9) * mm});
            skPoint(sketch, "E143.visualSharp", {"position": v(-310, 99.9) * mm});
            skArc(sketch, "E143.filletArc", {"start": v(-310, 101.9) * mm, "mid": v(-309.41, 100.49) * mm, "end": v(-308, 99.9) * mm});
            skPoint(sketch, "E144.visualSharp", {"position": v(-310, 58.9) * mm});
            skArc(sketch, "E144.filletArc", {"start": v(-308, 58.9) * mm, "mid": v(-309.41, 58.31) * mm, "end": v(-310, 56.9) * mm});
            skPoint(sketch, "E145.visualSharp", {"position": v(-310, 42.9) * mm});
            skArc(sketch, "E145.filletArc", {"start": v(-310, 44.9) * mm, "mid": v(-309.41, 43.49) * mm, "end": v(-308, 42.9) * mm});
            skPoint(sketch, "E146", {"position": v(-310, 89.4) * mm});
            skLineSegment(sketch, "E147", {"start": v(-290, 115.9) * mm, "end": v(-290, 42.9) * mm});
            skLineSegment(sketch, "E148", {"start": v(-310, 89.4) * mm, "end": v(-301.03, 89.4) * mm});
            skSolve(sketch);
        }
        {
            var Q0;
            Q0=makeQuery(id+"F30.imprint","IMPRINT",FACE,{"disambiguationData":[TD([[makeQuery(id+"F30.imprint","IMPRINT",EDGE,{"derivedFrom":sQuery(id+"F30.wireOp",EDGE,"E135")}),-1.0]])]});
            extrude(context, id + "F31", {"entities" : qUnion([Q0]), "operationType" : NewBodyOperationType.ADD, "oppositeDirection" : true, "depth" : 5 * mm});
        }
        {
            var Q0;
            Q0=qCreatedBy(id+"F26.planeOp",FACE);
            var sketch = newSketch(context, id + "F32", { "sketchPlane" : qUnion([Q0])});
            skLineSegment(sketch, "E149.bottom", {"start": v(-295, 23.5) * mm, "end": v(-318, 23.5) * mm});
            skLineSegment(sketch, "E149.top", {"start": v(-302, 98.5) * mm, "end": v(-318, 98.5) * mm});
            skLineSegment(sketch, "E149.left", {"start": v(-295, 23.5) * mm, "end": v(-295, 33.5) * mm});
            skLineSegment(sketch, "E149.right", {"start": v(-318, 23.5) * mm, "end": v(-318, 98.5) * mm});
            skLineSegment(sketch, "E150", {"start": v(-302, 98.5) * mm, "end": v(-302, 33.5) * mm});
            skLineSegment(sketch, "E151", {"start": v(-302, 33.5) * mm, "end": v(-295, 33.5) * mm});
            skCircle(sketch, "E152", {"center": v(-310, 48.5) * mm, "radius": 4.95 * mm});
            skCircle(sketch, "E153", {"center": v(-310, 88.5) * mm, "radius": 4.95 * mm});
            skSolve(sketch);
        }
        {
            var Q0;
            Q0=makeQuery(id+"F32.imprint","IMPRINT",FACE,{"disambiguationData":[TD([[makeQuery(id+"F32.imprint","IMPRINT",EDGE,{"derivedFrom":sQuery(id+"F32.wireOp",EDGE,"E149.bottom")}),-1.0]])]});
            extrude(context, id + "F33", {"entities" : qUnion([Q0]), "depth" : 5 * mm});
        }
    });
